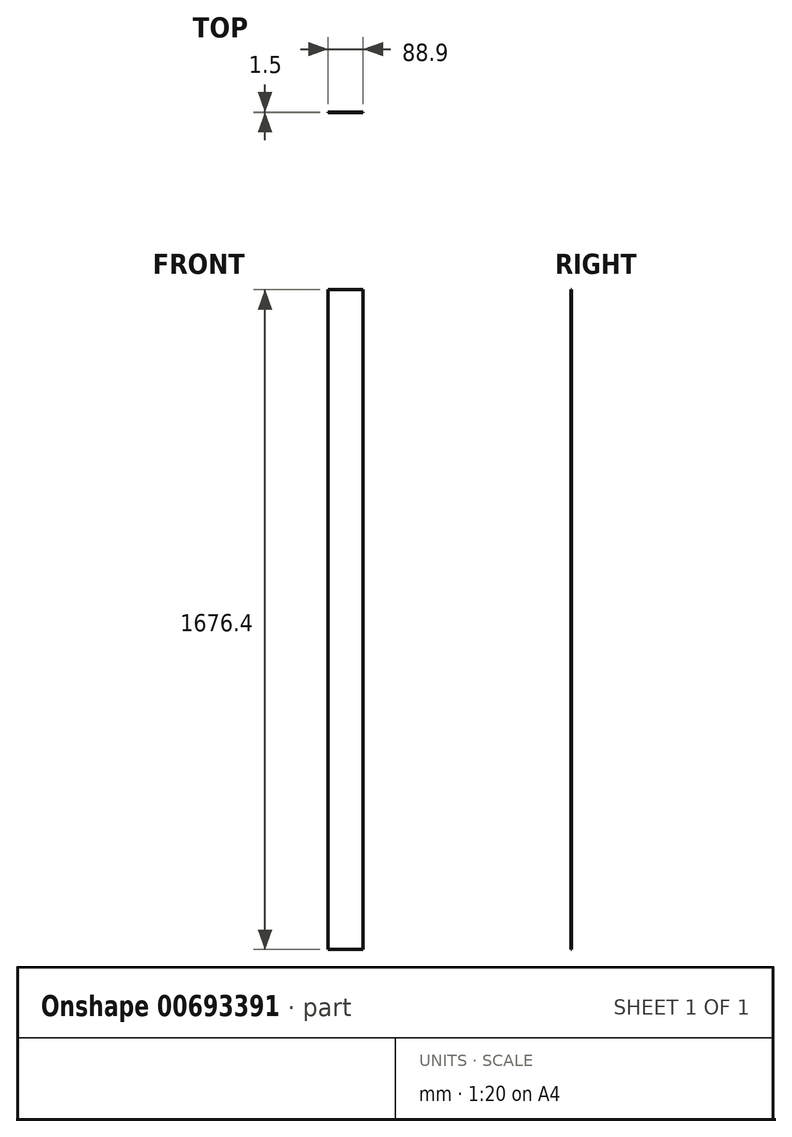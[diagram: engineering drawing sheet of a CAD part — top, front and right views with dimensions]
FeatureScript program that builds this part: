
annotation { "Feature Type Name" : "Feature", "Feature Type Description" : "" }
export const myFeature = defineFeature(function(context is Context, id is Id, definition is map)
    precondition{}
    {
        {
            assignVariable(context, id + "F0", {"name" : "W", "anyValue" : 1.5});
        }
        {
            var Q0;
            Q0=qCreatedBy(makeId("Front.planeOp"),FACE);
            var sketch = newSketch(context, id + "F1", { "sketchPlane" : qUnion([Q0])});
            skLineSegment(sketch, "E0.bottom", {"start": v(-173.4, 1449.68) * mm, "end": v(-84.5, 1449.68) * mm});
            skLineSegment(sketch, "E0.top", {"start": v(-173.4, -226.72) * mm, "end": v(-84.5, -226.72) * mm});
            skLineSegment(sketch, "E0.left", {"start": v(-173.4, 1449.68) * mm, "end": v(-173.4, -226.72) * mm});
            skLineSegment(sketch, "E0.right", {"start": v(-84.5, 1449.68) * mm, "end": v(-84.5, -226.72) * mm});
            skSolve(sketch);
        }
        {
            var Q0;
            Q0 = qSketchRegion(id + "F1", true);
            extrude(context, id + "F2", {"entities" : qUnion([Q0]), "depth" : (getVariable(context, 'W')) * mm, "offsetDistance" : 25.4 * mm});
        }
    });
